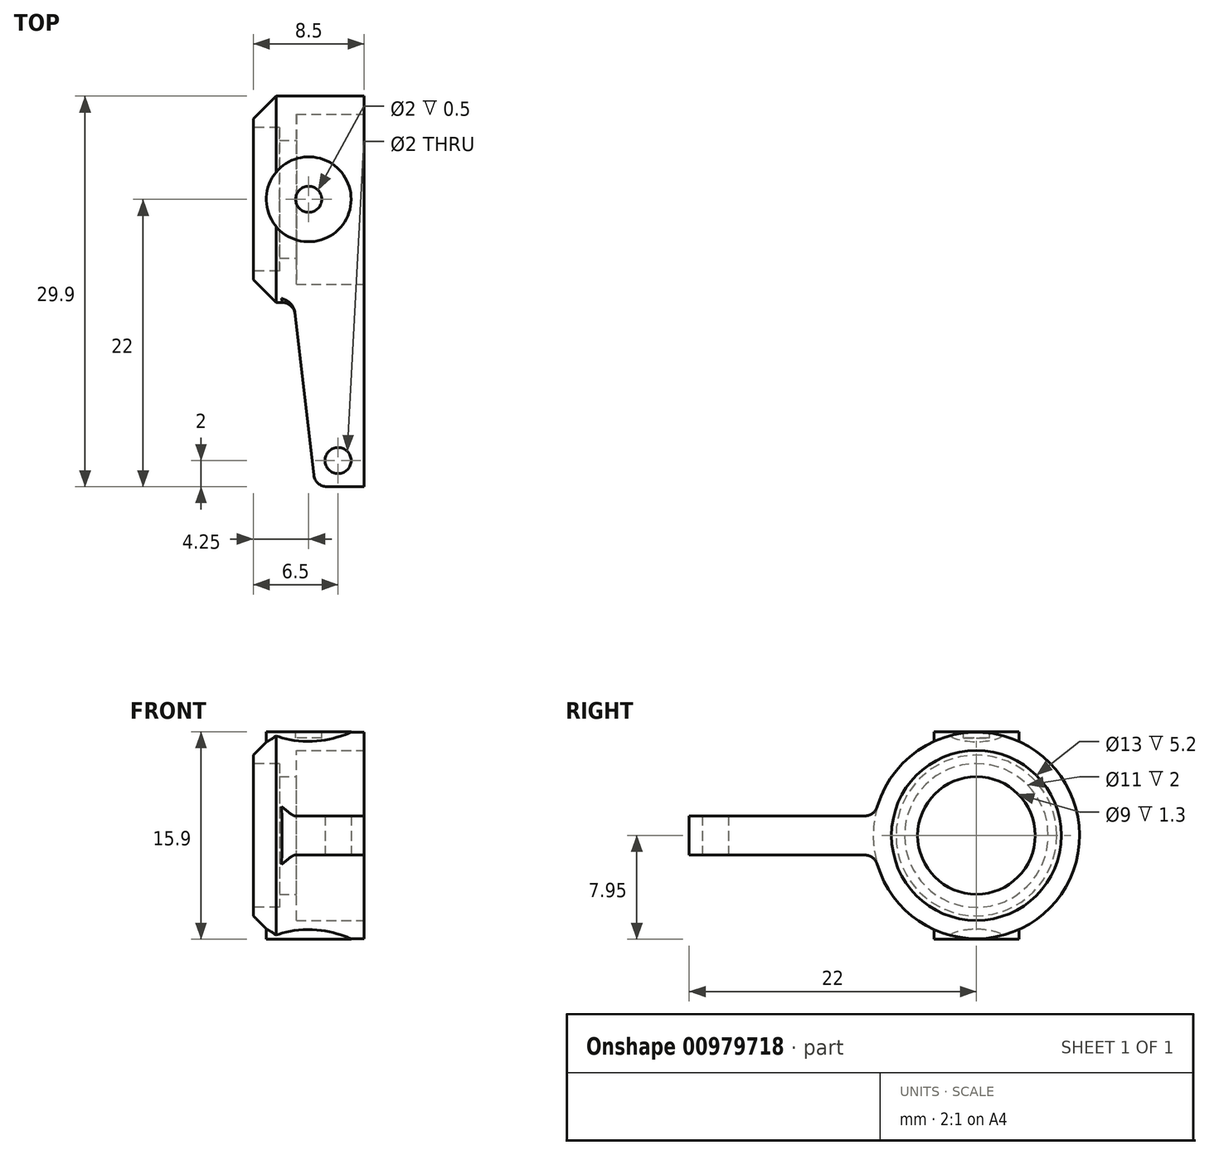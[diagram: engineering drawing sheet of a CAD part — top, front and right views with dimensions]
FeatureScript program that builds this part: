
annotation { "Feature Type Name" : "Feature", "Feature Type Description" : "" }
export const myFeature = defineFeature(function(context is Context, id is Id, definition is map)
    precondition{}
    {
        {
            var Q0;
            Q0=qCreatedBy(makeId("Right.planeOp"),FACE);
            var sketch = newSketch(context, id + "F0", { "sketchPlane" : qUnion([Q0])});
            skCircle(sketch, "E0", {"center": v(0, 0) * mm, "radius": 7.9 * mm});
            skSolve(sketch);
        }
        {
            var Q0;
            Q0 = qSketchRegion(id + "F0", true);
            extrude(context, id + "F1", {"entities" : qUnion([Q0]), "endBound" : BoundingType.SYMMETRIC, "depth" : 8.5 * mm, "offsetDistance" : 25 * mm});
        }
        {
            var Q0;
            Q0=qCreatedBy(makeId("Top.planeOp"),FACE);
            var sketch = newSketch(context, id + "F2", { "sketchPlane" : qUnion([Q0])});
            skCircle(sketch, "E1", {"center": v(0, 0) * mm, "radius": 3.25 * mm});
            skSolve(sketch);
        }
        {
            var Q0;
            Q0 = qSketchRegion(id + "F2", true);
            extrude(context, id + "F3", {"entities" : qUnion([Q0]), "operationType" : NewBodyOperationType.ADD, "endBound" : BoundingType.SYMMETRIC, "depth" : 15.9 * mm, "offsetDistance" : 25 * mm});
        }
        {
            var Q0;
            Q0=makeQuery(id+"F1.opExtrude","CAP_FACE",FACE,{"disambiguationData":[OSD([sQuery(id+"F0.wireOp",EDGE,"E0")])],"isStart":false});
            var sketch = newSketch(context, id + "F4", { "sketchPlane" : qUnion([Q0])});
            skCircle(sketch, "E2", {"center": v(0, 0) * mm, "radius": 6.5 * mm});
            skSolve(sketch);
        }
        {
            var Q0;
            Q0 = qSketchRegion(id + "F4", true);
            extrude(context, id + "F5", {"entities" : qUnion([Q0]), "operationType" : NewBodyOperationType.REMOVE, "oppositeDirection" : true, "depth" : 5.2 * mm, "offsetDistance" : 25 * mm});
        }
        {
            var Q0;
            Q0=makeQuery(id+"F1.opExtrude","CAP_FACE",FACE,{"disambiguationData":[OSD([sQuery(id+"F0.wireOp",EDGE,"E0")])],"isStart":true});
            var sketch = newSketch(context, id + "F6", { "sketchPlane" : qUnion([Q0])});
            skCircle(sketch, "E3", {"center": v(0, 0) * mm, "radius": 5.5 * mm});
            skSolve(sketch);
        }
        {
            var Q0;
            Q0 = qSketchRegion(id + "F6", true);
            extrude(context, id + "F7", {"entities" : qUnion([Q0]), "operationType" : NewBodyOperationType.REMOVE, "oppositeDirection" : true, "depth" : 2 * mm, "offsetDistance" : 25 * mm});
        }
        {
            var Q0;
            Q0=makeQuery(id+"F1.opExtrude","CAP_FACE",FACE,{"disambiguationData":[OSD([sQuery(id+"F0.wireOp",EDGE,"E0")])],"isStart":false});
            var sketch = newSketch(context, id + "F8", { "sketchPlane" : qUnion([Q0])});
            skCircle(sketch, "E4", {"center": v(0, 0) * mm, "radius": 4.5 * mm});
            skSolve(sketch);
        }
        {
            var Q0;
            Q0 = qSketchRegion(id + "F8", true);
            extrude(context, id + "F9", {"entities" : qUnion([Q0]), "operationType" : NewBodyOperationType.REMOVE, "endBound" : BoundingType.THROUGH_ALL, "oppositeDirection" : true, "depth" : 25 * mm, "offsetDistance" : 25 * mm});
        }
        {
            var Q0;
            Q0=makeQuery(id+"F1.opExtrude","CAP_EDGE",EDGE,{"disambiguationData":[OSD([sQuery(id+"F0.wireOp",EDGE,"E0")])],"isStart":true});
            chamfer(context, id + "F10", {"entities" : qUnion([Q0]), "width" : 1.75 * mm, "tangentPropagation" : true});
        }
        {
            var Q0;
            Q0=qCreatedBy(makeId("Top.planeOp"),FACE);
            var sketch = newSketch(context, id + "F11", { "sketchPlane" : qUnion([Q0])});
            skLineSegment(sketch, "E5.bottom", {"start": v(0.5, -22) * mm, "end": v(4.25, -22) * mm});
            skLineSegment(sketch, "E5.top", {"start": v(-1.25, -7) * mm, "end": v(4.25, -7) * mm});
            skLineSegment(sketch, "E5.right", {"start": v(4.25, -22) * mm, "end": v(4.25, -7) * mm});
            skPoint(sketch, "E6.centerSnap0", {"position": v(2.38, -22) * mm});
            skLineSegment(sketch, "E7", {"start": v(0.5, -22) * mm, "end": v(-1.25, -7) * mm});
            skSolve(sketch);
        }
        {
            var Q0;
            Q0 = qSketchRegion(id + "F11", true);
            extrude(context, id + "F12", {"entities" : qUnion([Q0]), "operationType" : NewBodyOperationType.ADD, "endBound" : BoundingType.SYMMETRIC, "depth" : 3 * mm, "offsetDistance" : 25 * mm});
        }
        {
            var Q0;
            Q0=makeQuery(id+"F12.boolean.opBoolean","INTERSECT",EDGE,{"derivedFrom":[makeQuery(id+"F1.opExtrude","SWEPT_FACE",FACE,{"disambiguationData":[OSD([sQuery(id+"F0.wireOp",EDGE,"E0")])]}),makeQuery(id+"F12.opExtrude","SWEPT_FACE",FACE,{"disambiguationData":[OSD([sQuery(id+"F11.wireOp",EDGE,"E7")])]})]});
            var Q1;
            Q1=makeQuery(id+"F12.boolean.opBoolean","INTERSECT",EDGE,{"derivedFrom":[makeQuery(id+"F1.opExtrude","SWEPT_FACE",FACE,{"disambiguationData":[OSD([sQuery(id+"F0.wireOp",EDGE,"E0")])]}),makeQuery(id+"F12.opExtrude","CAP_FACE",FACE,{"disambiguationData":[OSD([sQuery(id+"F11.wireOp",EDGE,"E5.bottom"),sQuery(id+"F11.wireOp",EDGE,"E5.top"),sQuery(id+"F11.wireOp",EDGE,"E5.right"),sQuery(id+"F11.wireOp",EDGE,"E7")])],"isStart":false})]});
            var Q2;
            Q2=makeQuery(id+"F12.boolean.opBoolean","INTERSECT",EDGE,{"derivedFrom":[makeQuery(id+"F1.opExtrude","SWEPT_FACE",FACE,{"disambiguationData":[OSD([sQuery(id+"F0.wireOp",EDGE,"E0")])]}),makeQuery(id+"F12.opExtrude","CAP_FACE",FACE,{"disambiguationData":[OSD([sQuery(id+"F11.wireOp",EDGE,"E5.bottom"),sQuery(id+"F11.wireOp",EDGE,"E5.top"),sQuery(id+"F11.wireOp",EDGE,"E5.right"),sQuery(id+"F11.wireOp",EDGE,"E7")])],"isStart":true})]});
            fillet(context, id + "F13", {"entities" : qUnion([Q0, Q1, Q2]), "radius" : 1 * mm, "tangentPropagation" : true, "allowEdgeOverflow" : false});
        }
        {
            var Q0;
            Q0=makeQuery(id+"F3.opExtrude","CAP_FACE",FACE,{"disambiguationData":[OSD([sQuery(id+"F2.wireOp",EDGE,"E1")])],"isStart":false});
            var sketch = newSketch(context, id + "F14", { "sketchPlane" : qUnion([Q0])});
            skCircle(sketch, "E8", {"center": v(0, 0) * mm, "radius": 1 * mm});
            skSolve(sketch);
        }
        {
            var Q0;
            Q0 = qSketchRegion(id + "F14", true);
            extrude(context, id + "F15", {"entities" : qUnion([Q0]), "operationType" : NewBodyOperationType.REMOVE, "oppositeDirection" : true, "depth" : 0.5 * mm, "offsetDistance" : 25 * mm});
        }
        {
            var Q0;
            Q0=qCreatedBy(makeId("Top.planeOp"),FACE);
            var sketch = newSketch(context, id + "F16", { "sketchPlane" : qUnion([Q0])});
            skCircle(sketch, "E9", {"center": v(2.25, -20) * mm, "radius": 1 * mm});
            skSolve(sketch);
        }
        {
            var Q0;
            Q0 = qSketchRegion(id + "F16", true);
            extrude(context, id + "F17", {"entities" : qUnion([Q0]), "operationType" : NewBodyOperationType.REMOVE, "endBound" : BoundingType.SYMMETRIC, "depth" : 8 * mm, "offsetDistance" : 25 * mm});
        }
        {
            var Q0;
            Q0=makeQuery(id+"F12.opExtrude","SWEPT_EDGE",EDGE,{"disambiguationData":[OSD([sQuery(id+"F11.wireOp",EDGE,"E5.bottom"),sQuery(id+"F11.wireOp",EDGE,"E7")])]});
            fillet(context, id + "F18", {"entities" : qUnion([Q0]), "radius" : 1 * mm, "tangentPropagation" : true, "allowEdgeOverflow" : false});
        }
    });
